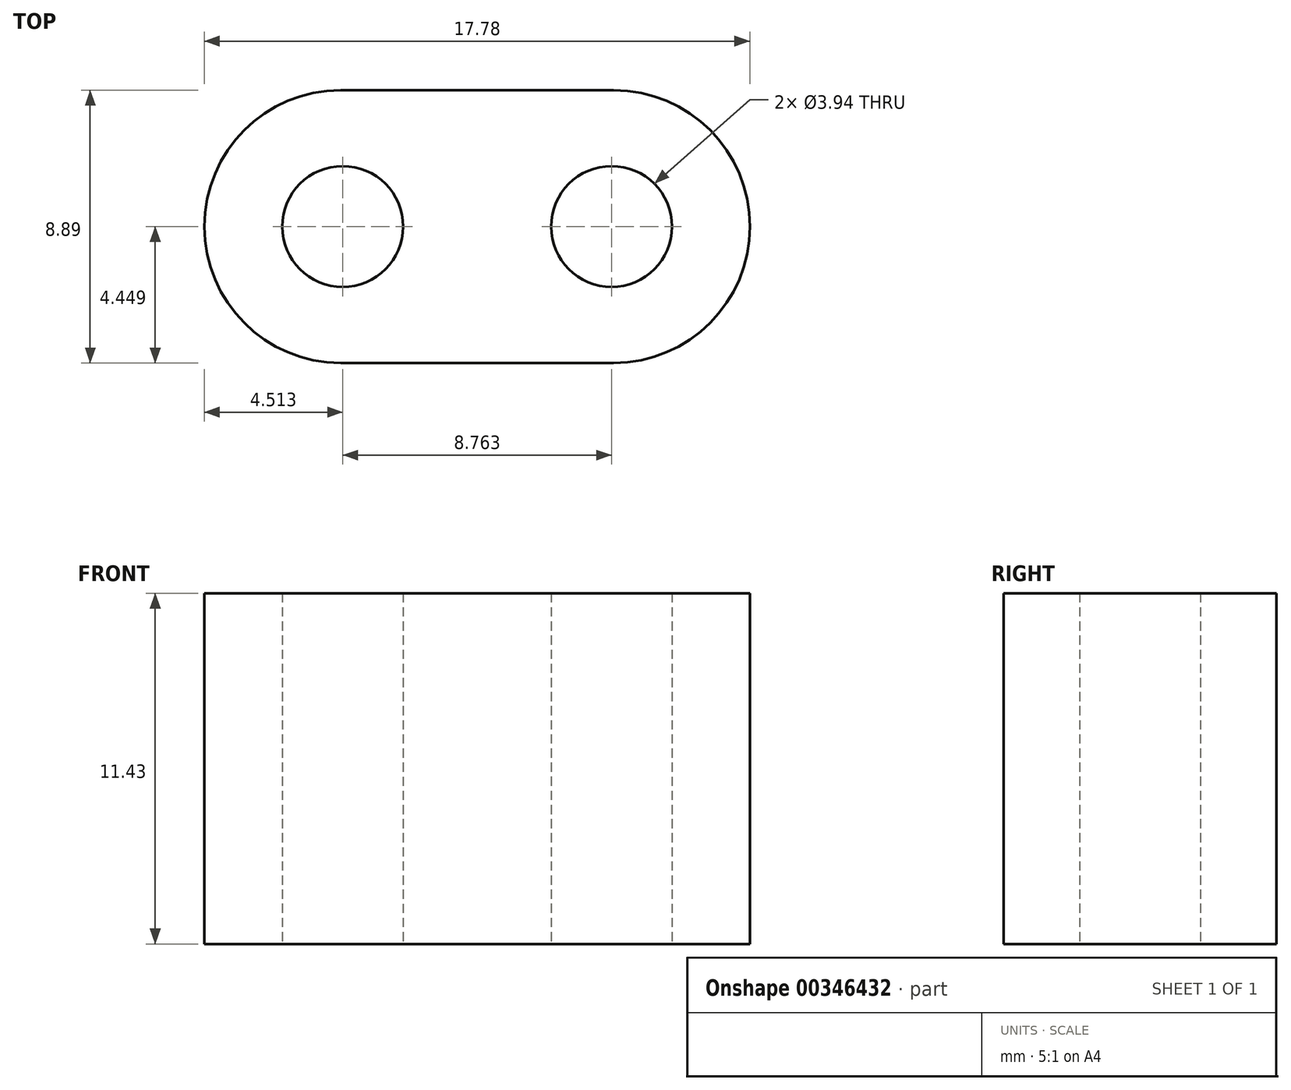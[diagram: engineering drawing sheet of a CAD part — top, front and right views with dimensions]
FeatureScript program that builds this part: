
annotation { "Feature Type Name" : "Feature", "Feature Type Description" : "" }
export const myFeature = defineFeature(function(context is Context, id is Id, definition is map)
    precondition{}
    {
        {
            var Q0;
            Q0=qCreatedBy(makeId("Top.planeOp"),FACE);
            var sketch = newSketch(context, id + "F0", { "sketchPlane" : qUnion([Q0])});
            skLineSegment(sketch, "E0.bottom", {"start": v(-127.84, 37.37) * mm, "end": v(-110.06, 37.37) * mm});
            skLineSegment(sketch, "E0.top", {"start": v(-127.84, 28.48) * mm, "end": v(-110.06, 28.48) * mm});
            skLineSegment(sketch, "E0.left", {"start": v(-127.84, 37.37) * mm, "end": v(-127.84, 28.48) * mm});
            skLineSegment(sketch, "E0.right", {"start": v(-110.06, 37.37) * mm, "end": v(-110.06, 28.48) * mm});
            skPoint(sketch, "E1.startSnap0", {"position": v(-118.95, 37.37) * mm});
            skPoint(sketch, "E1.startSnap1", {"position": v(-127.84, 32.93) * mm});
            skCircle(sketch, "E2", {"center": v(-123.33, 32.93) * mm, "radius": 1.97 * mm});
            skCircle(sketch, "E3", {"center": v(-114.56, 32.93) * mm, "radius": 1.97 * mm});
            skPoint(sketch, "E3.centerSnap0", {"position": v(-123.4, 32.93) * mm});
            skSolve(sketch);
        }
        {
            var Q0;
            Q0 = qSketchRegion(id + "F0", true);
            extrude(context, id + "F1", {"entities" : qUnion([Q0]), "depth" : 11.43 * mm});
        }
        {
            var Q0;
            Q0=makeQuery(id+"F1.opExtrude","SWEPT_EDGE",EDGE,{"disambiguationData":[OSD([sQuery(id+"F0.wireOp",EDGE,"E0.bottom"),sQuery(id+"F0.wireOp",EDGE,"E0.left")])]});
            var Q1;
            Q1=makeQuery(id+"F1.opExtrude","SWEPT_EDGE",EDGE,{"disambiguationData":[OSD([sQuery(id+"F0.wireOp",EDGE,"E0.bottom"),sQuery(id+"F0.wireOp",EDGE,"E0.right")])]});
            var Q2;
            Q2=makeQuery(id+"F1.opExtrude","SWEPT_EDGE",EDGE,{"disambiguationData":[OSD([sQuery(id+"F0.wireOp",EDGE,"E0.top"),sQuery(id+"F0.wireOp",EDGE,"E0.right")])]});
            var Q3;
            Q3=makeQuery(id+"F1.opExtrude","SWEPT_EDGE",EDGE,{"disambiguationData":[OSD([sQuery(id+"F0.wireOp",EDGE,"E0.top"),sQuery(id+"F0.wireOp",EDGE,"E0.left")])]});
            fillet(context, id + "F2", {"entities" : qUnion([Q0, Q1, Q2, Q3]), "radius" : 4.44 * mm, "tangentPropagation" : true, "allowEdgeOverflow" : false});
        }
    });
